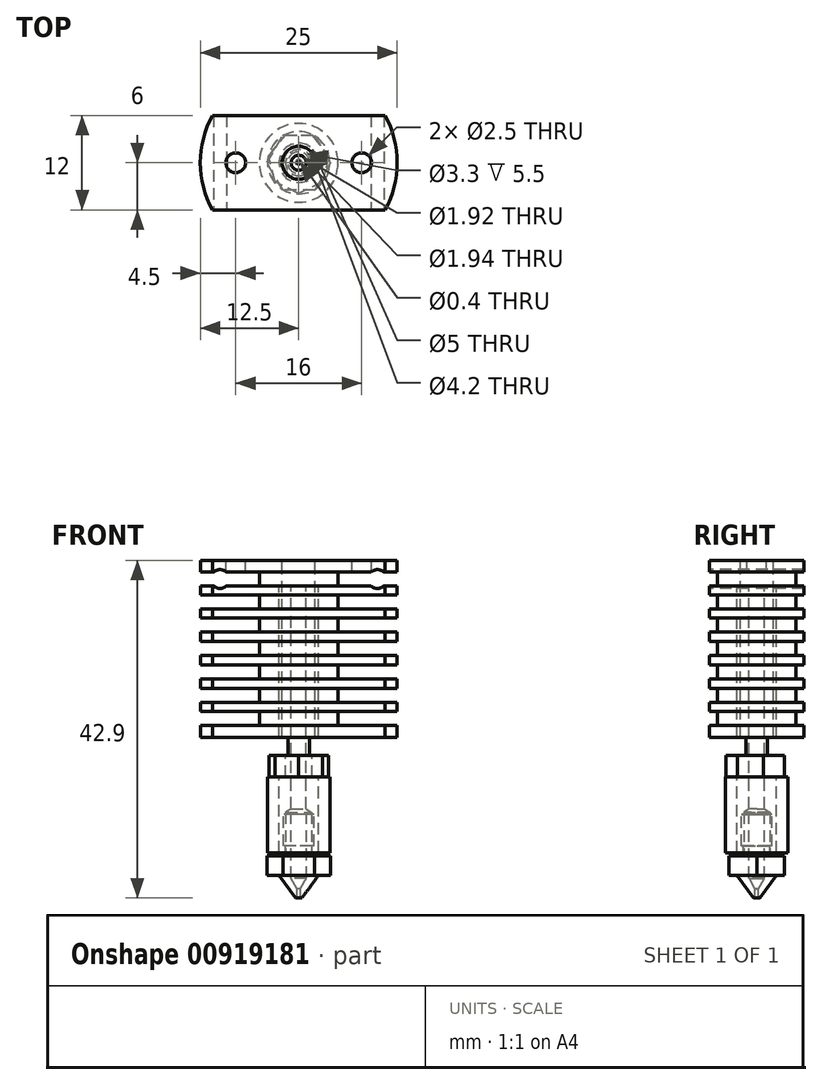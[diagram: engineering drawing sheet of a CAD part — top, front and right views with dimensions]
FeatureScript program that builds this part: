
annotation { "Feature Type Name" : "Feature", "Feature Type Description" : "" }
export const myFeature = defineFeature(function(context is Context, id is Id, definition is map)
    precondition{}
    {
        {
            var Q0;
            Q0=qCreatedBy(makeId("Front.planeOp"),FACE);
            var sketch = newSketch(context, id + "F0", { "sketchPlane" : qUnion([Q0])});
            skLineSegment(sketch, "E0.bottom", {"start": v(0, 0) * mm, "end": v(5, 0) * mm});
            skLineSegment(sketch, "E0.top", {"start": v(0, -22.5) * mm, "end": v(5, -22.5) * mm});
            skLineSegment(sketch, "E0.left", {"start": v(0, 0) * mm, "end": v(0, -22.5) * mm});
            skLineSegment(sketch, "E0.right", {"start": v(5, 0) * mm, "end": v(5, -22.5) * mm});
            skLineSegment(sketch, "E1", {"start": v(0, 43.67) * mm, "end": v(0, -73.74) * mm, "construction": true});
            skLineSegment(sketch, "E2.bottom", {"start": v(0, 0) * mm, "end": v(12.5, 0) * mm});
            skLineSegment(sketch, "E2.top", {"start": v(0, -1.5) * mm, "end": v(12.5, -1.5) * mm});
            skLineSegment(sketch, "E2.left", {"start": v(0, 0) * mm, "end": v(0, -1.5) * mm});
            skLineSegment(sketch, "E2.right", {"start": v(12.5, 0) * mm, "end": v(12.5, -1.5) * mm});
            skLineSegment(sketch, "E3.bottom", {"start": v(0, -3.27) * mm, "end": v(12.5, -3.27) * mm});
            skLineSegment(sketch, "E3.top", {"start": v(0, -4.42) * mm, "end": v(12.5, -4.42) * mm});
            skLineSegment(sketch, "E3.left", {"start": v(0, -3.27) * mm, "end": v(0, -4.42) * mm});
            skLineSegment(sketch, "E3.right", {"start": v(12.5, -3.27) * mm, "end": v(12.5, -4.42) * mm});
            skLineSegment(sketch, "E4.bottom", {"start": v(0, -6.2) * mm, "end": v(12.5, -6.2) * mm});
            skLineSegment(sketch, "E4.top", {"start": v(0, -7.34) * mm, "end": v(12.5, -7.34) * mm});
            skLineSegment(sketch, "E4.left", {"start": v(0, -6.2) * mm, "end": v(0, -7.34) * mm});
            skLineSegment(sketch, "E4.right", {"start": v(12.5, -6.2) * mm, "end": v(12.5, -7.34) * mm});
            skLineSegment(sketch, "E5.bottom", {"start": v(0, -9.11) * mm, "end": v(12.5, -9.11) * mm});
            skLineSegment(sketch, "E5.top", {"start": v(0, -10.31) * mm, "end": v(12.5, -10.31) * mm});
            skLineSegment(sketch, "E5.left", {"start": v(0, -9.11) * mm, "end": v(0, -10.31) * mm});
            skLineSegment(sketch, "E5.right", {"start": v(12.5, -9.11) * mm, "end": v(12.5, -10.31) * mm});
            skLineSegment(sketch, "E6.bottom", {"start": v(0, -12.09) * mm, "end": v(12.5, -12.09) * mm});
            skLineSegment(sketch, "E6.top", {"start": v(0, -13.29) * mm, "end": v(12.5, -13.29) * mm});
            skLineSegment(sketch, "E6.left", {"start": v(0, -12.09) * mm, "end": v(0, -13.29) * mm});
            skLineSegment(sketch, "E6.right", {"start": v(12.5, -12.09) * mm, "end": v(12.5, -13.29) * mm});
            skLineSegment(sketch, "E7.bottom", {"start": v(0, -15.06) * mm, "end": v(12.5, -15.06) * mm});
            skLineSegment(sketch, "E7.top", {"start": v(0, -16.26) * mm, "end": v(12.5, -16.26) * mm});
            skLineSegment(sketch, "E7.left", {"start": v(0, -15.06) * mm, "end": v(0, -16.26) * mm});
            skLineSegment(sketch, "E7.right", {"start": v(12.5, -15.06) * mm, "end": v(12.5, -16.26) * mm});
            skLineSegment(sketch, "E8.bottom", {"start": v(0, -18.03) * mm, "end": v(12.5, -18.03) * mm});
            skLineSegment(sketch, "E8.top", {"start": v(0, -19.23) * mm, "end": v(12.5, -19.23) * mm});
            skLineSegment(sketch, "E8.left", {"start": v(0, -18.03) * mm, "end": v(0, -19.23) * mm});
            skLineSegment(sketch, "E8.right", {"start": v(12.5, -18.03) * mm, "end": v(12.5, -19.23) * mm});
            skLineSegment(sketch, "E9.bottom", {"start": v(0, -21) * mm, "end": v(12.5, -21) * mm});
            skLineSegment(sketch, "E9.top", {"start": v(0, -22.5) * mm, "end": v(12.5, -22.5) * mm});
            skLineSegment(sketch, "E9.left", {"start": v(0, -21) * mm, "end": v(0, -22.5) * mm});
            skLineSegment(sketch, "E9.right", {"start": v(12.5, -21) * mm, "end": v(12.5, -22.5) * mm});
            skLineSegment(sketch, "E10", {"start": v(12.5, -21) * mm, "end": v(12.5, -19.23) * mm, "construction": true});
            skLineSegment(sketch, "E11", {"start": v(12.5, -18.03) * mm, "end": v(12.5, -16.26) * mm, "construction": true});
            skLineSegment(sketch, "E12", {"start": v(12.5, -15.06) * mm, "end": v(12.5, -13.29) * mm, "construction": true});
            skLineSegment(sketch, "E13", {"start": v(12.5, -12.09) * mm, "end": v(12.5, -10.31) * mm, "construction": true});
            skLineSegment(sketch, "E14", {"start": v(12.5, -9.11) * mm, "end": v(12.5, -7.34) * mm, "construction": true});
            skLineSegment(sketch, "E15", {"start": v(12.5, -6.2) * mm, "end": v(12.5, -4.42) * mm, "construction": true});
            skLineSegment(sketch, "E16", {"start": v(12.5, -3.27) * mm, "end": v(12.5, -1.5) * mm, "construction": true});
            skSolve(sketch);
        }
        {
            var Q0;
            Q0=qSketchRegion(id+"F0",true);
            var Q1;
            Q1=sQuery(id+"F0.wireOp",EDGE,"E1");
            revolve(context, id + "F1", {"entities" : qUnion([Q0]), "axis" : qUnion([Q1]), "revolveType" : RevolveType.FULL});
        }
        {
            var Q0;
            Q0=qCreatedBy(makeId("Top.planeOp"),FACE);
            var sketch = newSketch(context, id + "F2", { "sketchPlane" : qUnion([Q0])});
            skLineSegment(sketch, "E17.bottom", {"start": v(-10.97, -6) * mm, "end": v(10.97, -6) * mm});
            skLineSegment(sketch, "E17.top", {"start": v(-10.97, -12.5) * mm, "end": v(10.97, -12.5) * mm});
            skLineSegment(sketch, "E17.left", {"start": v(-10.97, -6) * mm, "end": v(-10.97, -12.5) * mm});
            skLineSegment(sketch, "E17.right", {"start": v(10.97, -6) * mm, "end": v(10.97, -12.5) * mm});
            skLineSegment(sketch, "E18.bottom", {"start": v(-10.97, 6) * mm, "end": v(10.97, 6) * mm});
            skLineSegment(sketch, "E18.top", {"start": v(-10.97, 12.5) * mm, "end": v(10.97, 12.5) * mm});
            skLineSegment(sketch, "E18.left", {"start": v(-10.97, 6) * mm, "end": v(-10.97, 12.5) * mm});
            skLineSegment(sketch, "E18.right", {"start": v(10.97, 6) * mm, "end": v(10.97, 12.5) * mm});
            skSolve(sketch);
        }
        {
            var Q0;
            Q0=qSketchRegion(id+"F2",true);
            extrude(context, id + "F3", {"entities" : qUnion([Q0]), "operationType" : NewBodyOperationType.REMOVE, "endBound" : BoundingType.THROUGH_ALL, "oppositeDirection" : true, "depth" : 25 * mm});
        }
        {
            var Q0;
            Q0=makeQuery(id+"F1.opRevolve","SWEPT_FACE",FACE,{"disambiguationData":[OSD([sQuery(id+"F0.wireOp",EDGE,"E2.bottom")])]});
            var sketch = newSketch(context, id + "F4", { "sketchPlane" : qUnion([Q0])});
            skPoint(sketch, "E19", {"position": v(0, 0) * mm});
            skPoint(sketch, "E20", {"position": v(-8, 0) * mm});
            skPoint(sketch, "E21", {"position": v(8, 0) * mm});
            skSolve(sketch);
        }
        {
            var Q0;
            Q0=sQuery(id+"F4.wireOp",VERTEX,"E19");
            var Q1;
            Q1=makeQuery(id+"F1.opRevolve","SWEPT_BODY",BODY,{"disambiguationData":[OSD([sQuery(id+"F0.wireOp",EDGE,"E0.left"),sQuery(id+"F0.wireOp",EDGE,"E0.right"),sQuery(id+"F0.wireOp",EDGE,"E2.bottom"),sQuery(id+"F0.wireOp",EDGE,"E2.top"),sQuery(id+"F0.wireOp",EDGE,"E2.left"),sQuery(id+"F0.wireOp",EDGE,"E2.right"),sQuery(id+"F0.wireOp",EDGE,"E3.bottom"),sQuery(id+"F0.wireOp",EDGE,"E3.top"),sQuery(id+"F0.wireOp",EDGE,"E3.left"),sQuery(id+"F0.wireOp",EDGE,"E3.right"),sQuery(id+"F0.wireOp",EDGE,"E4.bottom"),sQuery(id+"F0.wireOp",EDGE,"E4.top"),sQuery(id+"F0.wireOp",EDGE,"E4.left"),sQuery(id+"F0.wireOp",EDGE,"E4.right"),sQuery(id+"F0.wireOp",EDGE,"E5.bottom"),sQuery(id+"F0.wireOp",EDGE,"E5.top"),sQuery(id+"F0.wireOp",EDGE,"E5.left"),sQuery(id+"F0.wireOp",EDGE,"E5.right"),sQuery(id+"F0.wireOp",EDGE,"E6.bottom"),sQuery(id+"F0.wireOp",EDGE,"E6.top"),sQuery(id+"F0.wireOp",EDGE,"E6.left"),sQuery(id+"F0.wireOp",EDGE,"E6.right"),sQuery(id+"F0.wireOp",EDGE,"E7.bottom"),sQuery(id+"F0.wireOp",EDGE,"E7.top"),sQuery(id+"F0.wireOp",EDGE,"E7.left"),sQuery(id+"F0.wireOp",EDGE,"E7.right"),sQuery(id+"F0.wireOp",EDGE,"E8.bottom"),sQuery(id+"F0.wireOp",EDGE,"E8.top"),sQuery(id+"F0.wireOp",EDGE,"E8.left"),sQuery(id+"F0.wireOp",EDGE,"E8.right"),sQuery(id+"F0.wireOp",EDGE,"E9.bottom"),sQuery(id+"F0.wireOp",EDGE,"E9.top"),sQuery(id+"F0.wireOp",EDGE,"E9.left"),sQuery(id+"F0.wireOp",EDGE,"E9.right")])]});
            hole(context, id + "F5", {"style" : HoleStyle.SIMPLE, "endStyle" : HoleEndStyle.THROUGH, "standardTappedOrClearance" : lookupTablePath({ "standard" : "ISO", "engagement" : "75%", "pitch" : "0.8 mm", "size" : "M5", "type" : "Tapped" }), "standardBlindInLast" : lookupTablePath({ "standard" : "ISO", "engagement" : "75%", "pitch" : "0.8 mm", "size" : "M5", "type" : "Tapped" }), "holeDiameter" : 4.2 * mm, "locations" : qUnion([Q0]), "scope" : qUnion([Q1]), "isTappedThrough" : true, "majorDiameter" : 5 * mm, "showTappedDepth" : true});
        }
        {
            var Q0;
            Q0=sQuery(id+"F4.wireOp",VERTEX,"E20");
            var Q1;
            Q1=sQuery(id+"F4.wireOp",VERTEX,"E21");
            var Q2;
            Q2=makeQuery(id+"F1.opRevolve","SWEPT_BODY",BODY,{"disambiguationData":[OSD([sQuery(id+"F0.wireOp",EDGE,"E0.left"),sQuery(id+"F0.wireOp",EDGE,"E0.right"),sQuery(id+"F0.wireOp",EDGE,"E2.bottom"),sQuery(id+"F0.wireOp",EDGE,"E2.top"),sQuery(id+"F0.wireOp",EDGE,"E2.left"),sQuery(id+"F0.wireOp",EDGE,"E2.right"),sQuery(id+"F0.wireOp",EDGE,"E3.bottom"),sQuery(id+"F0.wireOp",EDGE,"E3.top"),sQuery(id+"F0.wireOp",EDGE,"E3.left"),sQuery(id+"F0.wireOp",EDGE,"E3.right"),sQuery(id+"F0.wireOp",EDGE,"E4.bottom"),sQuery(id+"F0.wireOp",EDGE,"E4.top"),sQuery(id+"F0.wireOp",EDGE,"E4.left"),sQuery(id+"F0.wireOp",EDGE,"E4.right"),sQuery(id+"F0.wireOp",EDGE,"E5.bottom"),sQuery(id+"F0.wireOp",EDGE,"E5.top"),sQuery(id+"F0.wireOp",EDGE,"E5.left"),sQuery(id+"F0.wireOp",EDGE,"E5.right"),sQuery(id+"F0.wireOp",EDGE,"E6.bottom"),sQuery(id+"F0.wireOp",EDGE,"E6.top"),sQuery(id+"F0.wireOp",EDGE,"E6.left"),sQuery(id+"F0.wireOp",EDGE,"E6.right"),sQuery(id+"F0.wireOp",EDGE,"E7.bottom"),sQuery(id+"F0.wireOp",EDGE,"E7.top"),sQuery(id+"F0.wireOp",EDGE,"E7.left"),sQuery(id+"F0.wireOp",EDGE,"E7.right"),sQuery(id+"F0.wireOp",EDGE,"E8.bottom"),sQuery(id+"F0.wireOp",EDGE,"E8.top"),sQuery(id+"F0.wireOp",EDGE,"E8.left"),sQuery(id+"F0.wireOp",EDGE,"E8.right"),sQuery(id+"F0.wireOp",EDGE,"E9.bottom"),sQuery(id+"F0.wireOp",EDGE,"E9.top"),sQuery(id+"F0.wireOp",EDGE,"E9.left"),sQuery(id+"F0.wireOp",EDGE,"E9.right")])]});
            hole(context, id + "F6", {"style" : HoleStyle.SIMPLE, "endStyle" : HoleEndStyle.BLIND, "standardTappedOrClearance" : lookupTablePath({ "standard" : "ISO", "engagement" : "75%", "pitch" : "0.5 mm", "size" : "M3", "type" : "Tapped" }), "standardBlindInLast" : lookupTablePath({ "standard" : "ISO", "engagement" : "75%", "pitch" : "0.5 mm", "size" : "M3", "type" : "Tapped" }), "holeDiameter" : 2.5 * mm, "holeDepth" : 2 * mm, "startFromSketch" : true, "locations" : qUnion([Q0, Q1]), "scope" : qUnion([Q2]), "majorDiameter" : 3 * mm});
        }
        {
            var Q0;
            Q0=qCreatedBy(makeId("Front.planeOp"),FACE);
            var sketch = newSketch(context, id + "F7", { "sketchPlane" : qUnion([Q0])});
            skLineSegment(sketch, "E22.bottom", {"start": v(0, -3.22) * mm, "end": v(1.39, -3.22) * mm});
            skLineSegment(sketch, "E22.top", {"start": v(0, -37.5) * mm, "end": v(1.39, -37.5) * mm});
            skLineSegment(sketch, "E22.left", {"start": v(0, -3.22) * mm, "end": v(0, -37.5) * mm});
            skLineSegment(sketch, "E22.right", {"start": v(1.38, -3.22) * mm, "end": v(1.39, -37.5) * mm});
            skLineSegment(sketch, "E23", {"start": v(0, 12.08) * mm, "end": v(0, -40.12) * mm, "construction": true});
            skLineSegment(sketch, "E24.bottom", {"start": v(0, -37.5) * mm, "end": v(2.5, -37.5) * mm});
            skLineSegment(sketch, "E24.top", {"start": v(0, -24.8) * mm, "end": v(2.5, -24.8) * mm});
            skLineSegment(sketch, "E24.left", {"start": v(0, -37.5) * mm, "end": v(0, -24.8) * mm});
            skLineSegment(sketch, "E24.right", {"start": v(2.5, -37.5) * mm, "end": v(2.5, -24.8) * mm});
            skLineSegment(sketch, "E25.bottom", {"start": v(0, -3.22) * mm, "end": v(2.5, -3.22) * mm});
            skLineSegment(sketch, "E25.top", {"start": v(0, -22.5) * mm, "end": v(2.5, -22.5) * mm});
            skLineSegment(sketch, "E25.left", {"start": v(0, -3.22) * mm, "end": v(0, -22.5) * mm});
            skLineSegment(sketch, "E25.right", {"start": v(2.5, -3.22) * mm, "end": v(2.5, -22.5) * mm});
            skSolve(sketch);
        }
        {
            var Q0;
            Q0=qSketchRegion(id+"F7",true);
            var Q1;
            Q1=sQuery(id+"F7.wireOp",EDGE,"E23");
            revolve(context, id + "F8", {"entities" : qUnion([Q0]), "axis" : qUnion([Q1]), "revolveType" : RevolveType.FULL});
        }
        {
            var Q0;
            Q0=makeQuery(id+"F8.opRevolve","SWEPT_FACE",FACE,{"disambiguationData":[OSD([sQuery(id+"F7.wireOp",EDGE,"E24.top")])]});
            var sketch = newSketch(context, id + "F9", { "sketchPlane" : qUnion([Q0])});
            skCircle(sketch, "E26.cCircle", {"center": v(0, 0) * mm, "radius": 3.5 * mm, "construction": true});
            skLineSegment(sketch, "E26.0", {"start": v(1.69, 3.5) * mm, "end": v(3.79, 0.86) * mm});
            skLineSegment(sketch, "E26.1", {"start": v(3.79, 0.86) * mm, "end": v(3.04, -2.42) * mm});
            skLineSegment(sketch, "E26.2", {"start": v(3.04, -2.42) * mm, "end": v(0, -3.88) * mm});
            skLineSegment(sketch, "E26.3", {"start": v(0, -3.88) * mm, "end": v(-3.04, -2.42) * mm});
            skLineSegment(sketch, "E26.4", {"start": v(-3.04, -2.42) * mm, "end": v(-3.79, 0.86) * mm});
            skLineSegment(sketch, "E26.5", {"start": v(-3.79, 0.86) * mm, "end": v(-1.69, 3.5) * mm});
            skLineSegment(sketch, "E26.6", {"start": v(-1.69, 3.5) * mm, "end": v(1.69, 3.5) * mm});
            skPoint(sketch, "E26.0.midPoint", {"position": v(2.74, 2.18) * mm});
            skSolve(sketch);
        }
        {
            var Q0;
            Q0=qSketchRegion(id+"F9",true);
            extrude(context, id + "F10", {"entities" : qUnion([Q0]), "operationType" : NewBodyOperationType.ADD, "oppositeDirection" : true, "depth" : 2.75 * mm});
        }
        {
            var Q0;
            Q0=makeQuery(id+"F8.opRevolve","SWEPT_FACE",FACE,{"disambiguationData":[OSD([sQuery(id+"F7.wireOp",EDGE,"E24.bottom")])]});
            var sketch = newSketch(context, id + "F11", { "sketchPlane" : qUnion([Q0])});
            skPoint(sketch, "E27", {"position": v(0, 0) * mm});
            skSolve(sketch);
        }
        {
            var Q0;
            Q0=sQuery(id+"F11.wireOp",VERTEX,"E27");
            var Q1;
            Q1=makeQuery(id+"F8.opRevolve","SWEPT_BODY",BODY,{"disambiguationData":[OSD([sQuery(id+"F7.wireOp",EDGE,"E22.left"),sQuery(id+"F7.wireOp",EDGE,"E22.right"),sQuery(id+"F7.wireOp",EDGE,"E24.bottom"),sQuery(id+"F7.wireOp",EDGE,"E24.top"),sQuery(id+"F7.wireOp",EDGE,"E24.left"),sQuery(id+"F7.wireOp",EDGE,"E24.right"),sQuery(id+"F7.wireOp",EDGE,"E25.bottom"),sQuery(id+"F7.wireOp",EDGE,"E25.top"),sQuery(id+"F7.wireOp",EDGE,"E25.left"),sQuery(id+"F7.wireOp",EDGE,"E25.right")])]});
            hole(context, id + "F12", {"style" : HoleStyle.SIMPLE, "endStyle" : HoleEndStyle.BLIND, "standardTappedOrClearance" : lookupTablePath({ "standard" : "ISO", "engagement" : "75%", "pitch" : "0.7 mm", "size" : "M4", "type" : "Tapped" }), "standardBlindInLast" : lookupTablePath({ "standard" : "ISO", "engagement" : "75%", "pitch" : "0.7 mm", "size" : "M4", "type" : "Tapped" }), "holeDiameter" : 3.3 * mm, "holeDepth" : 5.5 * mm, "startFromSketch" : true, "locations" : qUnion([Q0]), "scope" : qUnion([Q1]), "majorDiameter" : 4 * mm});
        }
        {
            var Q0;
            Q0=makeQuery(id+"F8.opRevolve","SWEPT_FACE",FACE,{"disambiguationData":[OSD([sQuery(id+"F7.wireOp",EDGE,"E25.bottom")])]});
            var sketch = newSketch(context, id + "F13", { "sketchPlane" : qUnion([Q0])});
            skCircle(sketch, "E28", {"center": v(0, 0) * mm, "radius": 0.96 * mm});
            skSolve(sketch);
        }
        {
            var Q0;
            Q0=qSketchRegion(id+"F13",true);
            extrude(context, id + "F14", {"entities" : qUnion([Q0]), "operationType" : NewBodyOperationType.REMOVE, "endBound" : BoundingType.THROUGH_ALL, "oppositeDirection" : true, "depth" : 25 * mm});
        }
        {
            var Q0;
            Q0=makeQuery(id+"F10.opExtrude","CAP_FACE",FACE,{"disambiguationData":[OSD([sQuery(id+"F9.wireOp",EDGE,"E26.0"),sQuery(id+"F9.wireOp",EDGE,"E26.1"),sQuery(id+"F9.wireOp",EDGE,"E26.2"),sQuery(id+"F9.wireOp",EDGE,"E26.3"),sQuery(id+"F9.wireOp",EDGE,"E26.4"),sQuery(id+"F9.wireOp",EDGE,"E26.5"),sQuery(id+"F9.wireOp",EDGE,"E26.6")])],"isStart":false});
            var sketch = newSketch(context, id + "F15", { "sketchPlane" : qUnion([Q0])});
            skCircle(sketch, "E29", {"center": v(0, 0) * mm, "radius": 2.5 * mm});
            skCircle(sketch, "E30", {"center": v(0, 0) * mm, "radius": 3.96 * mm});
            skSolve(sketch);
        }
        {
            var Q0;
            Q0=qSketchRegion(id+"F15",true);
            extrude(context, id + "F16", {"entities" : qUnion([Q0]), "depth" : 9.6 * mm});
        }
        {
            var Q0;
            Q0=qCreatedBy(makeId("Front.planeOp"),FACE);
            var sketch = newSketch(context, id + "F17", { "sketchPlane" : qUnion([Q0])});
            skLineSegment(sketch, "E31", {"start": v(0, 4.14) * mm, "end": v(0, -44.2) * mm, "construction": true});
            skLineSegment(sketch, "E32.bottom", {"start": v(0.97, -32.3) * mm, "end": v(1.95, -32.3) * mm});
            skLineSegment(sketch, "E32.top", {"start": v(0.2, -42.9) * mm, "end": v(0.41, -42.9) * mm});
            skLineSegment(sketch, "E32.right", {"start": v(3.5, -37.57) * mm, "end": v(3.5, -40.04) * mm});
            skLineSegment(sketch, "E33", {"start": v(3.5, -37.57) * mm, "end": v(1.67, -37.57) * mm});
            skLineSegment(sketch, "E34", {"start": v(1.67, -37.57) * mm, "end": v(1.67, -36.3) * mm});
            skLineSegment(sketch, "E35", {"start": v(1.67, -36.3) * mm, "end": v(1.95, -36.3) * mm});
            skLineSegment(sketch, "E36", {"start": v(1.95, -36.3) * mm, "end": v(1.95, -32.3) * mm});
            skLineSegment(sketch, "E37", {"start": v(3.5, -40.04) * mm, "end": v(2.5, -40.04) * mm});
            skLineSegment(sketch, "E38", {"start": v(2.5, -40.04) * mm, "end": v(0.41, -42.9) * mm});
            skLineSegment(sketch, "E39", {"start": v(0.2, -42.9) * mm, "end": v(0.2, -41.73) * mm});
            skLineSegment(sketch, "E40", {"start": v(0.2, -41.73) * mm, "end": v(0.97, -40.4) * mm});
            skLineSegment(sketch, "E41", {"start": v(0.97, -40.4) * mm, "end": v(0.97, -32.3) * mm});
            skPoint(sketch, "E41.endSnap0", {"position": v(0.97, -32.3) * mm});
            skPoint(sketch, "E42.orphan", {"position": v(0, -32.3) * mm});
            skSolve(sketch);
        }
        {
            var Q0;
            Q0=qSketchRegion(id+"F17",true);
            var Q1;
            Q1=sQuery(id+"F17.wireOp",EDGE,"E31");
            revolve(context, id + "F18", {"entities" : qUnion([Q0]), "axis" : qUnion([Q1]), "revolveType" : RevolveType.FULL});
        }
        {
            var Q0;
            Q0=makeQuery(id+"F18.opRevolve","SWEPT_FACE",FACE,{"disambiguationData":[OSD([sQuery(id+"F17.wireOp",EDGE,"E33")])]});
            var sketch = newSketch(context, id + "F19", { "sketchPlane" : qUnion([Q0])});
            skCircle(sketch, "E43.cCircle", {"center": v(0, 0) * mm, "radius": 3.5 * mm, "construction": true});
            skLineSegment(sketch, "E43.0", {"start": v(-2.02, -3.5) * mm, "end": v(-4.04, 0) * mm});
            skLineSegment(sketch, "E43.1", {"start": v(-4.04, 0) * mm, "end": v(-2.02, 3.5) * mm});
            skLineSegment(sketch, "E43.2", {"start": v(-2.02, 3.5) * mm, "end": v(2.02, 3.5) * mm});
            skLineSegment(sketch, "E43.3", {"start": v(2.02, 3.5) * mm, "end": v(4.04, 0) * mm});
            skLineSegment(sketch, "E43.4", {"start": v(4.04, 0) * mm, "end": v(2.02, -3.5) * mm});
            skLineSegment(sketch, "E43.5", {"start": v(2.02, -3.5) * mm, "end": v(-2.02, -3.5) * mm});
            skPoint(sketch, "E43.0.midPoint", {"position": v(-3.03, -1.75) * mm});
            skCircle(sketch, "E44.0", {"center": v(0, 0) * mm, "radius": 0.97 * mm});
            skSolve(sketch);
        }
        {
            var Q0;
            Q0=qSketchRegion(id+"F19",true);
            var Q1;
            Q1=makeQuery(id+"F18.opRevolve","SWEPT_FACE",FACE,{"disambiguationData":[OSD([sQuery(id+"F17.wireOp",EDGE,"E37")])]});
            extrude(context, id + "F20", {"entities" : qUnion([Q0]), "operationType" : NewBodyOperationType.ADD, "endBound" : BoundingType.UP_TO_SURFACE, "oppositeDirection" : true, "endBoundEntityFace" : qUnion([Q1]), "depth" : 25 * mm});
        }
        {
            var Q0;
            Q0=qCreatedBy(makeId("Front.planeOp"),FACE);
            var sketch = newSketch(context, id + "F21", { "sketchPlane" : qUnion([Q0])});
            skLineSegment(sketch, "E45", {"start": v(0, 6.79) * mm, "end": v(0, -19.22) * mm, "construction": true});
            skLineSegment(sketch, "E46.bottom", {"start": v(2.73, 11.3) * mm, "end": v(3.88, 11.3) * mm});
            skLineSegment(sketch, "E46.top", {"start": v(2.1, 0.8) * mm, "end": v(3.88, 0.8) * mm});
            skLineSegment(sketch, "E46.left", {"start": v(1.05, 1.8) * mm, "end": v(1.05, -3.2) * mm});
            skLineSegment(sketch, "E46.right", {"start": v(3.88, 11.3) * mm, "end": v(3.88, 0.8) * mm});
            skLineSegment(sketch, "E47.top", {"start": v(1.05, -3.2) * mm, "end": v(2.45, -3.2) * mm});
            skLineSegment(sketch, "E47.right", {"start": v(2.45, -0.05) * mm, "end": v(2.45, -3.2) * mm});
            skLineSegment(sketch, "E48", {"start": v(2.73, 11.3) * mm, "end": v(2.73, 1.8) * mm});
            skLineSegment(sketch, "E49", {"start": v(2.73, 1.8) * mm, "end": v(1.05, 1.8) * mm});
            skPoint(sketch, "E50.orphan", {"position": v(1.05, 11.3) * mm});
            skLineSegment(sketch, "E51", {"start": v(2.45, -0.05) * mm, "end": v(2.1, -0.05) * mm});
            skLineSegment(sketch, "E52", {"start": v(2.1, -0.05) * mm, "end": v(2.1, 0.8) * mm});
            skSolve(sketch);
        }
        {
            var Q0;
            Q0=qSketchRegion(id+"F21",true);
            var Q1;
            Q1=sQuery(id+"F21.wireOp",EDGE,"E45");
            revolve(context, id + "F22", {"entities" : qUnion([Q0]), "axis" : qUnion([Q1]), "revolveType" : RevolveType.FULL});
        }
        {
            var Q0;
            Q0=makeQuery(id+"F22.opRevolve","SWEPT_FACE",FACE,{"disambiguationData":[OSD([sQuery(id+"F21.wireOp",EDGE,"E46.top")])]});
            cPlane(context, id + "F23", {"entities" : qUnion([Q0]), "cplaneType" : CPlaneType.OFFSET, "offset" : 5.5 * mm, "oppositeDirection" : true, "width" : 150 * mm, "height" : 150 * mm});
        }
        {
            var Q0;
            Q0=qCreatedBy(id+"F23.planeOp",FACE);
            var sketch = newSketch(context, id + "F24", { "sketchPlane" : qUnion([Q0])});
            skCircle(sketch, "E53.cCircle", {"center": v(0, 0) * mm, "radius": 3.98 * mm, "construction": true});
            skLineSegment(sketch, "E53.0", {"start": v(-2.3, -3.97) * mm, "end": v(-4.59, 0) * mm});
            skLineSegment(sketch, "E53.1", {"start": v(-4.59, 0) * mm, "end": v(-2.3, 3.98) * mm});
            skLineSegment(sketch, "E53.2", {"start": v(-2.3, 3.98) * mm, "end": v(2.3, 3.98) * mm});
            skLineSegment(sketch, "E53.3", {"start": v(2.3, 3.97) * mm, "end": v(4.59, 0) * mm});
            skLineSegment(sketch, "E53.4", {"start": v(4.59, 0) * mm, "end": v(2.3, -3.98) * mm});
            skLineSegment(sketch, "E53.5", {"start": v(2.3, -3.97) * mm, "end": v(-2.3, -3.97) * mm});
            skPoint(sketch, "E53.0.midPoint", {"position": v(-3.44, -1.99) * mm});
            skCircle(sketch, "E54.0", {"center": v(0, 0) * mm, "radius": 2.73 * mm});
            skSolve(sketch);
        }
        {
            var Q0;
            Q0=qSketchRegion(id+"F24",true);
            extrude(context, id + "F25", {"entities" : qUnion([Q0]), "operationType" : NewBodyOperationType.ADD, "depth" : 4.22 * mm});
        }
        {
            var Q0;
            Q0=makeQuery(id+"F3.boolean.opBoolean","COPY",FACE,{"disambiguationData":[TD([makeQuery(id+"F1.opRevolve","SWEPT_FACE",FACE,{"disambiguationData":[OSD([sQuery(id+"F0.wireOp",EDGE,"E2.bottom")])]})])],"derivedFrom":makeQuery(id+"F3.opExtrude","SWEPT_FACE",FACE,{"disambiguationData":[OSD([sQuery(id+"F2.wireOp",EDGE,"E17.bottom")])]})});
            var sketch = newSketch(context, id + "F26", { "sketchPlane" : qUnion([Q0])});
            skPoint(sketch, "E55", {"position": v(-10, -2.39) * mm});
            skPoint(sketch, "E56", {"position": v(10, -2.39) * mm});
            skLineSegment(sketch, "E57", {"start": v(0, 10.11) * mm, "end": v(0, -7.87) * mm, "construction": true});
            skLineSegment(sketch, "E58", {"start": v(-10, -3.27) * mm, "end": v(-10, -1.5) * mm, "construction": true});
            skSolve(sketch);
        }
        {
            var Q0;
            Q0=sQuery(id+"F26.wireOp",VERTEX,"E55");
            var Q1;
            Q1=sQuery(id+"F26.wireOp",VERTEX,"E56");
            var Q2;
            Q2=makeQuery(id+"F1.opRevolve","SWEPT_BODY",BODY,{"disambiguationData":[OSD([sQuery(id+"F0.wireOp",EDGE,"E0.left"),sQuery(id+"F0.wireOp",EDGE,"E0.right"),sQuery(id+"F0.wireOp",EDGE,"E2.bottom"),sQuery(id+"F0.wireOp",EDGE,"E2.top"),sQuery(id+"F0.wireOp",EDGE,"E2.left"),sQuery(id+"F0.wireOp",EDGE,"E2.right"),sQuery(id+"F0.wireOp",EDGE,"E3.bottom"),sQuery(id+"F0.wireOp",EDGE,"E3.top"),sQuery(id+"F0.wireOp",EDGE,"E3.left"),sQuery(id+"F0.wireOp",EDGE,"E3.right"),sQuery(id+"F0.wireOp",EDGE,"E4.bottom"),sQuery(id+"F0.wireOp",EDGE,"E4.top"),sQuery(id+"F0.wireOp",EDGE,"E4.left"),sQuery(id+"F0.wireOp",EDGE,"E4.right"),sQuery(id+"F0.wireOp",EDGE,"E5.bottom"),sQuery(id+"F0.wireOp",EDGE,"E5.top"),sQuery(id+"F0.wireOp",EDGE,"E5.left"),sQuery(id+"F0.wireOp",EDGE,"E5.right"),sQuery(id+"F0.wireOp",EDGE,"E6.bottom"),sQuery(id+"F0.wireOp",EDGE,"E6.top"),sQuery(id+"F0.wireOp",EDGE,"E6.left"),sQuery(id+"F0.wireOp",EDGE,"E6.right"),sQuery(id+"F0.wireOp",EDGE,"E7.bottom"),sQuery(id+"F0.wireOp",EDGE,"E7.top"),sQuery(id+"F0.wireOp",EDGE,"E7.left"),sQuery(id+"F0.wireOp",EDGE,"E7.right"),sQuery(id+"F0.wireOp",EDGE,"E8.bottom"),sQuery(id+"F0.wireOp",EDGE,"E8.top"),sQuery(id+"F0.wireOp",EDGE,"E8.left"),sQuery(id+"F0.wireOp",EDGE,"E8.right"),sQuery(id+"F0.wireOp",EDGE,"E9.bottom"),sQuery(id+"F0.wireOp",EDGE,"E9.top"),sQuery(id+"F0.wireOp",EDGE,"E9.left"),sQuery(id+"F0.wireOp",EDGE,"E9.right")])]});
            hole(context, id + "F27", {"style" : HoleStyle.SIMPLE, "endStyle" : HoleEndStyle.THROUGH, "standardTappedOrClearance" : lookupTablePath({ "standard" : "ISO", "engagement" : "75%", "pitch" : "0.6 mm", "size" : "M3", "type" : "Tapped" }), "standardBlindInLast" : lookupTablePath({ "standard" : "ISO", "engagement" : "75%", "pitch" : "0.6 mm", "size" : "M3", "type" : "Tapped" }), "holeDiameter" : 2.4 * mm, "startFromSketch" : true, "locations" : qUnion([Q0, Q1]), "scope" : qUnion([Q2]), "isTappedThrough" : true, "showTappedDepth" : true});
        }
        {
            var Q0;
            Q0=qCreatedBy(makeId("Front.planeOp"),FACE);
            var sketch = newSketch(context, id + "F28", { "sketchPlane" : qUnion([Q0])});
            skLineSegment(sketch, "E59.top", {"start": v(3.88, 12.3) * mm, "end": v(2.47, 12.3) * mm});
            skLineSegment(sketch, "E59.left", {"start": v(3.88, 11.3) * mm, "end": v(3.88, 12.3) * mm});
            skLineSegment(sketch, "E60.bottom", {"start": v(3.88, 13.2) * mm, "end": v(2.47, 13.2) * mm});
            skLineSegment(sketch, "E60.left", {"start": v(3.88, 13.2) * mm, "end": v(3.88, 14.2) * mm});
            skLineSegment(sketch, "E61.left", {"start": v(2.47, 13.2) * mm, "end": v(2.47, 12.3) * mm});
            skLineSegment(sketch, "E61.right", {"start": v(2.1, 14.7) * mm, "end": v(2.1, 11.3) * mm});
            skLineSegment(sketch, "E62", {"start": v(3.38, 14.7) * mm, "end": v(2.1, 14.7) * mm});
            skLineSegment(sketch, "E63", {"start": v(3.88, 11.3) * mm, "end": v(2.1, 11.3) * mm});
            skLineSegment(sketch, "E64.0", {"start": v(0, 6.79) * mm, "end": v(0, -19.22) * mm, "construction": true});
            skPoint(sketch, "E65.visualSharp", {"position": v(3.88, 14.7) * mm});
            skArc(sketch, "E65.filletArc", {"start": v(3.88, 14.2) * mm, "mid": v(3.73, 14.55) * mm, "end": v(3.38, 14.7) * mm});
            skSolve(sketch);
        }
        {
            var Q0;
            Q0=qSketchRegion(id+"F28",true);
            var Q1;
            Q1=sQuery(id+"F28.wireOp",EDGE,"E64.0");
            revolve(context, id + "F29", {"entities" : qUnion([Q0]), "axis" : qUnion([Q1]), "revolveType" : RevolveType.FULL});
        }
        {
            var Q0;
            Q0=makeQuery(id+"F22.opRevolve","SWEPT_BODY",BODY,{"disambiguationData":[OSD([sQuery(id+"F21.wireOp",EDGE,"E46.bottom"),sQuery(id+"F21.wireOp",EDGE,"E46.top"),sQuery(id+"F21.wireOp",EDGE,"E46.left"),sQuery(id+"F21.wireOp",EDGE,"E46.right"),sQuery(id+"F21.wireOp",EDGE,"E47.top"),sQuery(id+"F21.wireOp",EDGE,"E47.right"),sQuery(id+"F21.wireOp",EDGE,"E48"),sQuery(id+"F21.wireOp",EDGE,"E49"),sQuery(id+"F21.wireOp",EDGE,"E51"),sQuery(id+"F21.wireOp",EDGE,"E52")])]});
            deleteBodies(context, id + "F30", {"entities" : qUnion([Q0])});
        }
        {
            var Q0;
            Q0=makeQuery(id+"F29.opRevolve","SWEPT_BODY",BODY,{"disambiguationData":[OSD([sQuery(id+"F28.wireOp",EDGE,"E59.top"),sQuery(id+"F28.wireOp",EDGE,"E59.left"),sQuery(id+"F28.wireOp",EDGE,"E60.bottom"),sQuery(id+"F28.wireOp",EDGE,"E60.left"),sQuery(id+"F28.wireOp",EDGE,"E61.left"),sQuery(id+"F28.wireOp",EDGE,"E61.right"),sQuery(id+"F28.wireOp",EDGE,"E62"),sQuery(id+"F28.wireOp",EDGE,"E63"),sQuery(id+"F28.wireOp",EDGE,"E65.filletArc")])]});
            deleteBodies(context, id + "F31", {"entities" : qUnion([Q0])});
        }
    });
